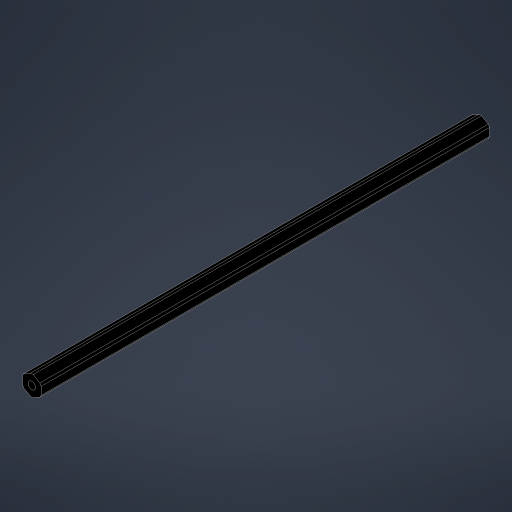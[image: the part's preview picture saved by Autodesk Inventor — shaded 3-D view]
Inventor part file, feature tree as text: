
AUTODESK INVENTOR PART (.ipt)
format: ipt  version: 2023.4 (Build 274418000, 418)  size: 196,608 bytes
history: native  units: in
note: dims shown in document units (in); Inventor stores cm internally (conversion verified against a paired STEP export)
features: extrude x2, projected_geometry x2, hole x1
ambient origin geometry x8: Origin, YZ Plane, XZ Plane, XY Plane, X Axis, Y Axis, Z Axis, Center Point
bodies: Solid1 (feature_tree)
feature tree (5):
  extrude  "Extrusion1"  TaperAngle=0.0deg  [1 undecoded]
  hole  "Hole1"  [1 undecoded]
  extrude  "Extrusion3"  TaperAngle=0.0deg  [1 undecoded]
  projected_geometry  "Project Cut Edges1"
  projected_geometry  "Project Cut Edges2"
note: 3 required parameter values undecoded (feature->parameter linkage not recoverable at this tier; creation-order binding heuristic only, values carry confidence <= 0.55)
